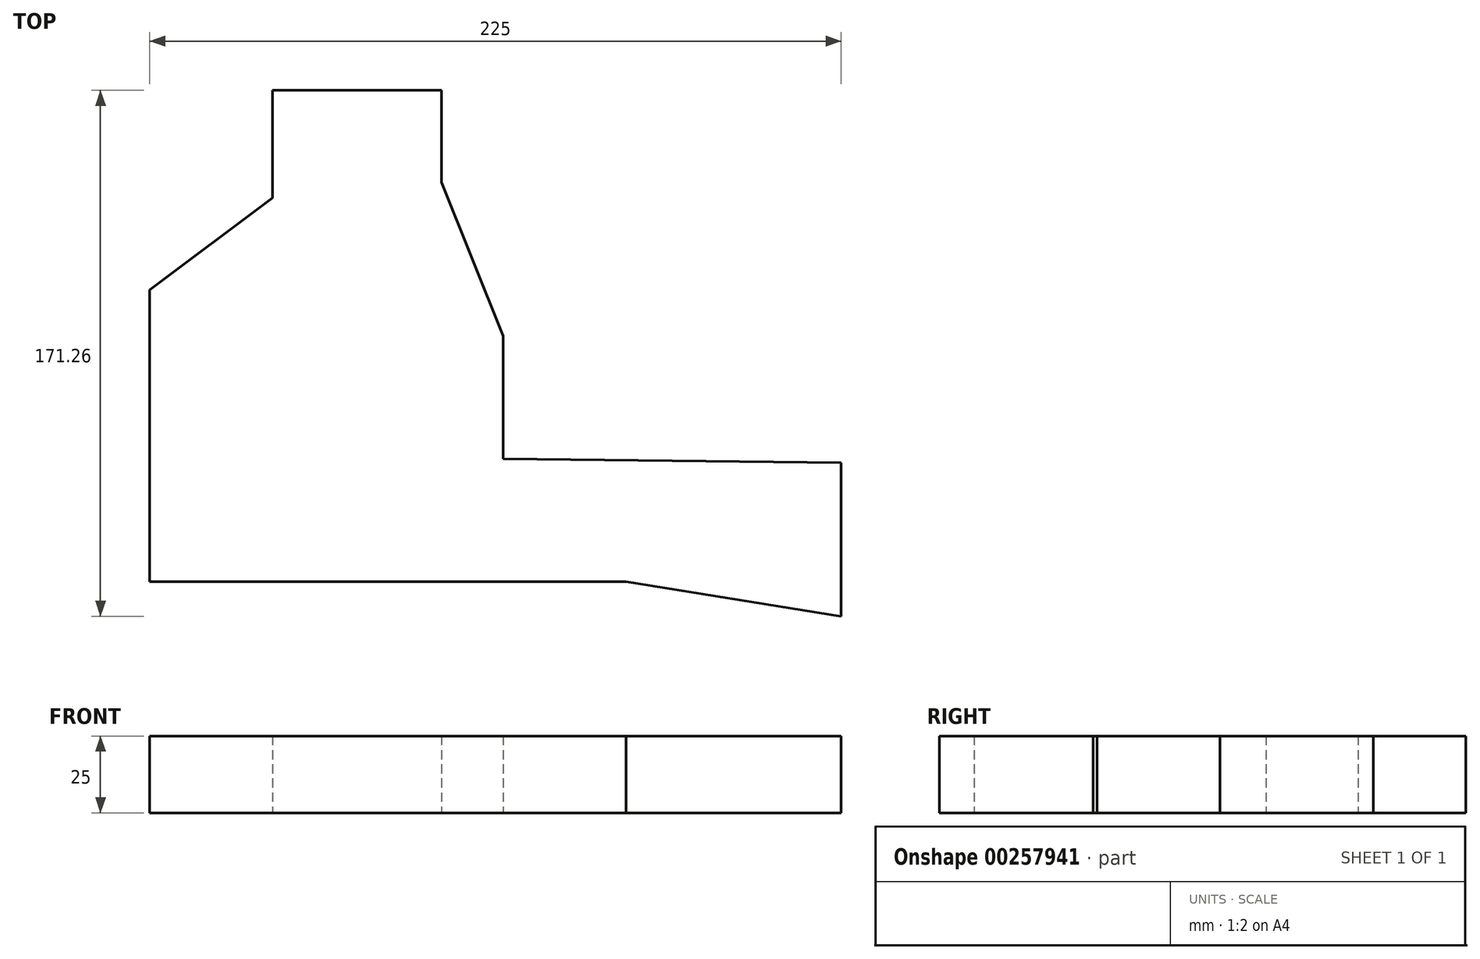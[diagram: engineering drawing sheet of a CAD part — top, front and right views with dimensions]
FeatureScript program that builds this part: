
annotation { "Feature Type Name" : "Feature", "Feature Type Description" : "" }
export const myFeature = defineFeature(function(context is Context, id is Id, definition is map)
    precondition{}
    {
        {
            var Q0;
            Q0=qCreatedBy(makeId("Top.planeOp"),FACE);
            var sketch = newSketch(context, id + "F0", { "sketchPlane" : qUnion([Q0])});
            skLineSegment(sketch, "E0", {"start": v(-104.44, -83.25) * mm, "end": v(50.56, -83.25) * mm});
            skLineSegment(sketch, "E1", {"start": v(50.56, -83.25) * mm, "end": v(120.56, -94.51) * mm});
            skLineSegment(sketch, "E2", {"start": v(-104.44, -83.25) * mm, "end": v(-104.44, 11.75) * mm});
            skLineSegment(sketch, "E3", {"start": v(-104.44, 11.75) * mm, "end": v(-64.44, 41.75) * mm});
            skLineSegment(sketch, "E4", {"start": v(-64.44, 41.75) * mm, "end": v(-64.44, 76.75) * mm});
            skLineSegment(sketch, "E5", {"start": v(-64.44, 76.75) * mm, "end": v(-9.44, 76.75) * mm});
            skLineSegment(sketch, "E6", {"start": v(-9.44, 76.75) * mm, "end": v(-9.44, 46.75) * mm});
            skLineSegment(sketch, "E7", {"start": v(-9.44, 46.75) * mm, "end": v(10.56, -3.25) * mm});
            skLineSegment(sketch, "E8", {"start": v(10.56, -3.25) * mm, "end": v(10.56, -43.25) * mm});
            skLineSegment(sketch, "E9", {"start": v(120.56, -94.51) * mm, "end": v(120.56, -44.51) * mm});
            skLineSegment(sketch, "E10", {"start": v(120.56, -44.51) * mm, "end": v(10.56, -43.25) * mm});
            skSolve(sketch);
        }
        {
            var Q0;
            Q0 = qSketchRegion(id + "F0", true);
            extrude(context, id + "F1", {"entities" : qUnion([Q0]), "depth" : 25 * mm});
        }
    });
